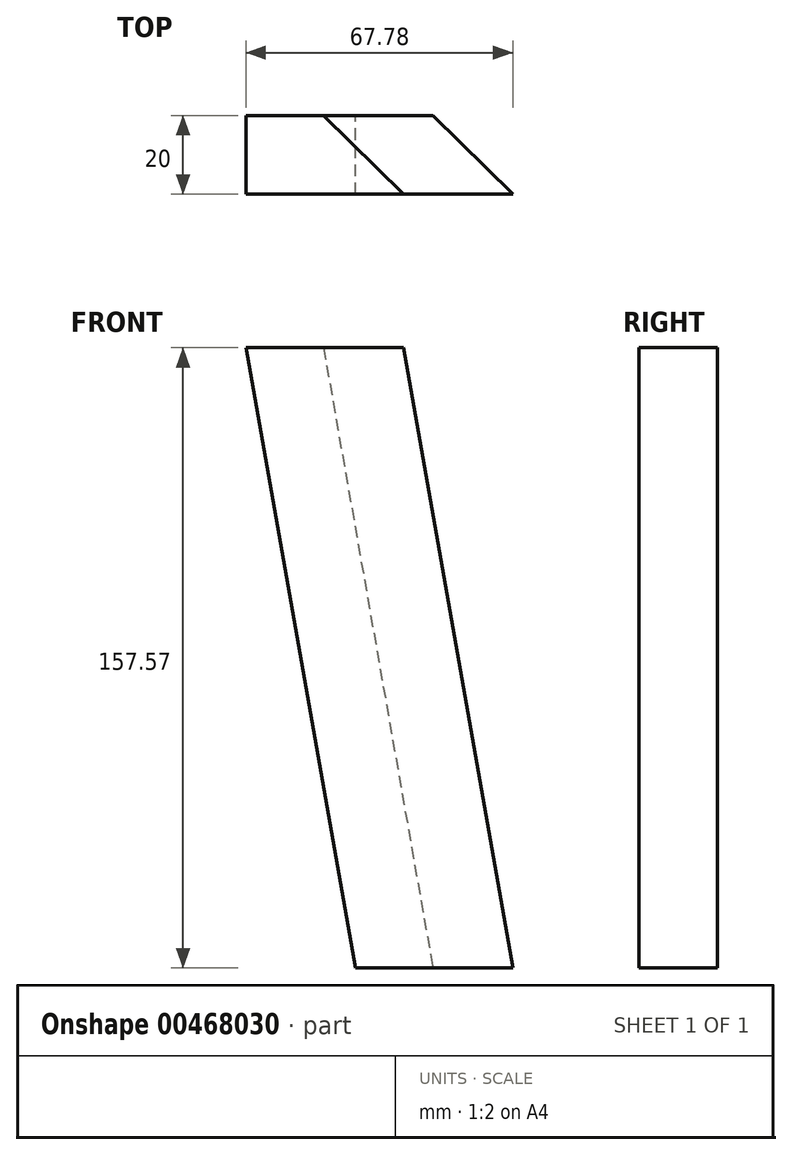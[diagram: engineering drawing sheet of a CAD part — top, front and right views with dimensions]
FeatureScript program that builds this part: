
annotation { "Feature Type Name" : "Feature", "Feature Type Description" : "" }
export const myFeature = defineFeature(function(context is Context, id is Id, definition is map)
    precondition{}
    {
        {
            var Q0;
            Q0=qCreatedBy(makeId("Front.planeOp"),FACE);
            var sketch = newSketch(context, id + "F0", { "sketchPlane" : qUnion([Q0])});
            skLineSegment(sketch, "E0", {"start": v(0, 0) * mm, "end": v(40, 0) * mm});
            skLineSegment(sketch, "E1", {"start": v(40, 0) * mm, "end": v(67.78, -157.57) * mm});
            skLineSegment(sketch, "E2", {"start": v(67.78, -157.57) * mm, "end": v(27.78, -157.57) * mm});
            skLineSegment(sketch, "E3", {"start": v(27.78, -157.57) * mm, "end": v(0, 0) * mm});
            skSolve(sketch);
        }
        {
            var Q0;
            Q0=makeQuery(id+"F0.imprint","IMPRINT",FACE,{"disambiguationData":[TD([[makeQuery(id+"F0.imprint","IMPRINT",EDGE,{"derivedFrom":sQuery(id+"F0.wireOp",EDGE,"E0")}),-1.0]])]});
            extrude(context, id + "F1", {"entities" : qUnion([Q0]), "depth" : 20 * mm, "offsetDistance" : 25 * mm});
        }
        {
            var Q0;
            Q0=makeQuery(id+"F1.opExtrude","CAP_EDGE",EDGE,{"disambiguationData":[OSD([sQuery(id+"F0.wireOp",EDGE,"E1")])],"isStart":true});
            chamfer(context, id + "F2", {"entities" : qUnion([Q0]), "width" : 20 * mm, "tangentPropagation" : true});
        }
    });
